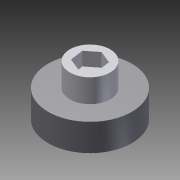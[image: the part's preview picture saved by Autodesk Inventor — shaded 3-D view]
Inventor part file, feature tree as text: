
AUTODESK INVENTOR PART (.ipt)
format: ipt  version: 2012 (Build 160160000, 160)  size: 816,640 bytes
history: native  units: mm
features: other x3, extrude x2, sketch x2, projected_geometry x1
ambient origin geometry x8: Origin, YZ Plane, XZ Plane, XY Plane, X Axis, Y Axis, Z Axis, Center Point
bodies: Solid1 (feature_tree)
feature tree (8):
  other  "MotorToGear.iam"
  other  "Spur Gear2:1"
  other  "MotorToGear.ipt:1"
  extrude  "Extrusion1"  Depth=10.0mm TaperAngle=0.0deg
  extrude  "Extrusion2"  [1 undecoded]
  sketch  "Sketch2"  dims[d0=10.0mm d1=10.0mm d2=0.0mm]
  sketch  "Sketch4"  dims[d3=10.0mm d4=0.0mm]
  projected_geometry  "Projected Loop1"
note: 1 required parameter value undecoded (feature->parameter linkage not recoverable at this tier; creation-order binding heuristic only, values carry confidence <= 0.55)
